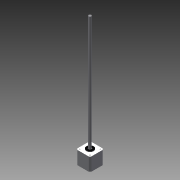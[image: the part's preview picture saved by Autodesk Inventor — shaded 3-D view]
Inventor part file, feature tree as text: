
AUTODESK INVENTOR PART (.ipt)
format: ipt  version: 2015 (Build 190159000, 159)  size: 139,264 bytes
history: native  units: mm
features: sketch x4, extrude x3, hole x1
ambient origin geometry x8: Origin, YZ Plane, XZ Plane, XY Plane, X Axis, Y Axis, Z Axis, Center Point
bodies: Solid1 (feature_tree)
feature tree (8):
  extrude  "Extrusion1"  Depth=42.3mm
  extrude  "Extrusion2"  TaperAngle=45.0deg  [1 undecoded]
  hole  "Hole1"  [1 undecoded]
  extrude  "Extrusion3"  Depth=10.0mm
  sketch  "Sketch1"  dims[d0=42.3mm d1=42.3mm]
  sketch  "Sketch2"  dims[d2=5.0mm d3=45.0deg]
  sketch  "Sketch3"  dims[d4=0.25mm d5=40.0mm d6=0.0mm]
  sketch  "Sketch4"  dims[d7=22.0mm d8=10.0mm d9=2.0mm d10=0.0mm d11=31.0mm d12=31.0mm d13=2.459mm d14=6.0mm d15=4.0mm d16=2.0mm d17=90.0deg d18=4.5mm d19=20.594885mm d20=8.0mm d21=350.0mm d22=0.0mm]
note: 2 required parameter values undecoded (feature->parameter linkage not recoverable at this tier; creation-order binding heuristic only, values carry confidence <= 0.55)
